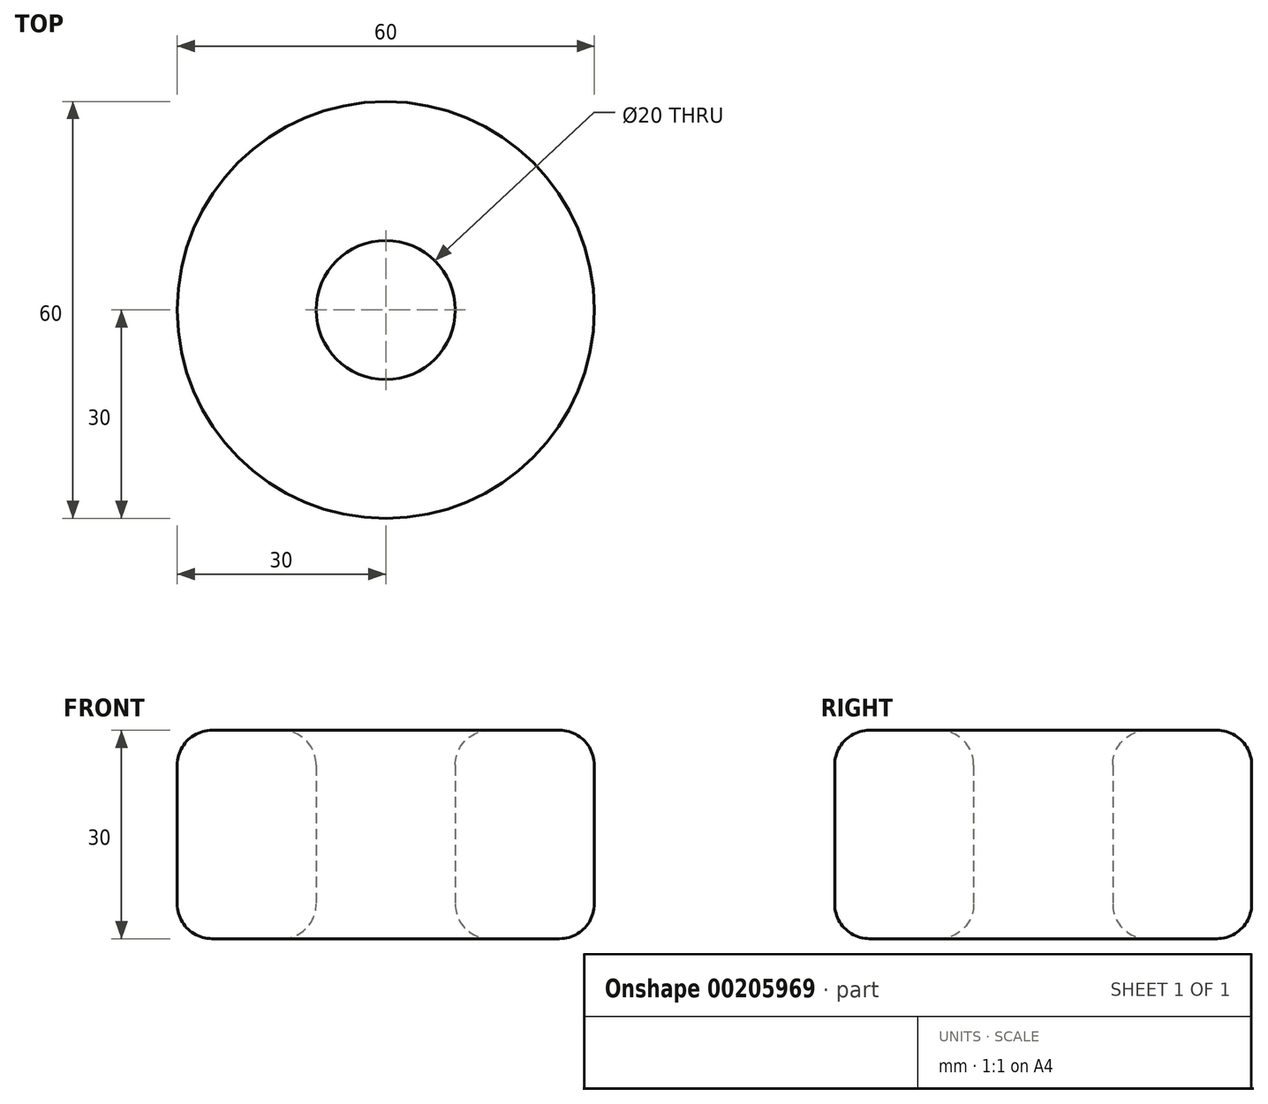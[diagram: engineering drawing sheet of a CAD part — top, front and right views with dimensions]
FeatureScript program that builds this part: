
annotation { "Feature Type Name" : "Feature", "Feature Type Description" : "" }
export const myFeature = defineFeature(function(context is Context, id is Id, definition is map)
    precondition{}
    {
        {
            var Q0;
            Q0=qCreatedBy(makeId("Front.planeOp"),FACE);
            var sketch = newSketch(context, id + "F0", { "sketchPlane" : qUnion([Q0])});
            skLineSegment(sketch, "E0.bottom", {"start": v(-25, 0) * mm, "end": v(-15, 0) * mm});
            skLineSegment(sketch, "E0.top", {"start": v(-25, 30) * mm, "end": v(-15, 30) * mm});
            skLineSegment(sketch, "E0.left", {"start": v(-30, 5) * mm, "end": v(-30, 25) * mm});
            skLineSegment(sketch, "E0.right", {"start": v(-10, 5) * mm, "end": v(-10, 25) * mm});
            skPoint(sketch, "E1.visualSharp", {"position": v(-30, 30) * mm});
            skArc(sketch, "E1.filletArc", {"start": v(-25, 30) * mm, "mid": v(-28.54, 28.54) * mm, "end": v(-30, 25) * mm});
            skPoint(sketch, "E2.visualSharp", {"position": v(-10, 30) * mm});
            skArc(sketch, "E2.filletArc", {"start": v(-10, 25) * mm, "mid": v(-11.46, 28.54) * mm, "end": v(-15, 30) * mm});
            skPoint(sketch, "E3.visualSharp", {"position": v(-10, 0) * mm});
            skArc(sketch, "E3.filletArc", {"start": v(-15, 0) * mm, "mid": v(-11.46, 1.46) * mm, "end": v(-10, 5) * mm});
            skPoint(sketch, "E4.visualSharp", {"position": v(-30, 0) * mm});
            skArc(sketch, "E4.filletArc", {"start": v(-30, 5) * mm, "mid": v(-28.54, 1.46) * mm, "end": v(-25, 0) * mm});
            skLineSegment(sketch, "E5", {"start": v(0, 0) * mm, "end": v(0, 55.18) * mm, "construction": true});
            skSolve(sketch);
        }
        {
            var Q0;
            Q0=qSketchRegion(id+"F0",true);
            var Q1;
            Q1=sQuery(id+"F0.wireOp",EDGE,"E5");
            revolve(context, id + "F1", {"entities" : qUnion([Q0]), "axis" : qUnion([Q1]), "revolveType" : RevolveType.FULL});
        }
    });
